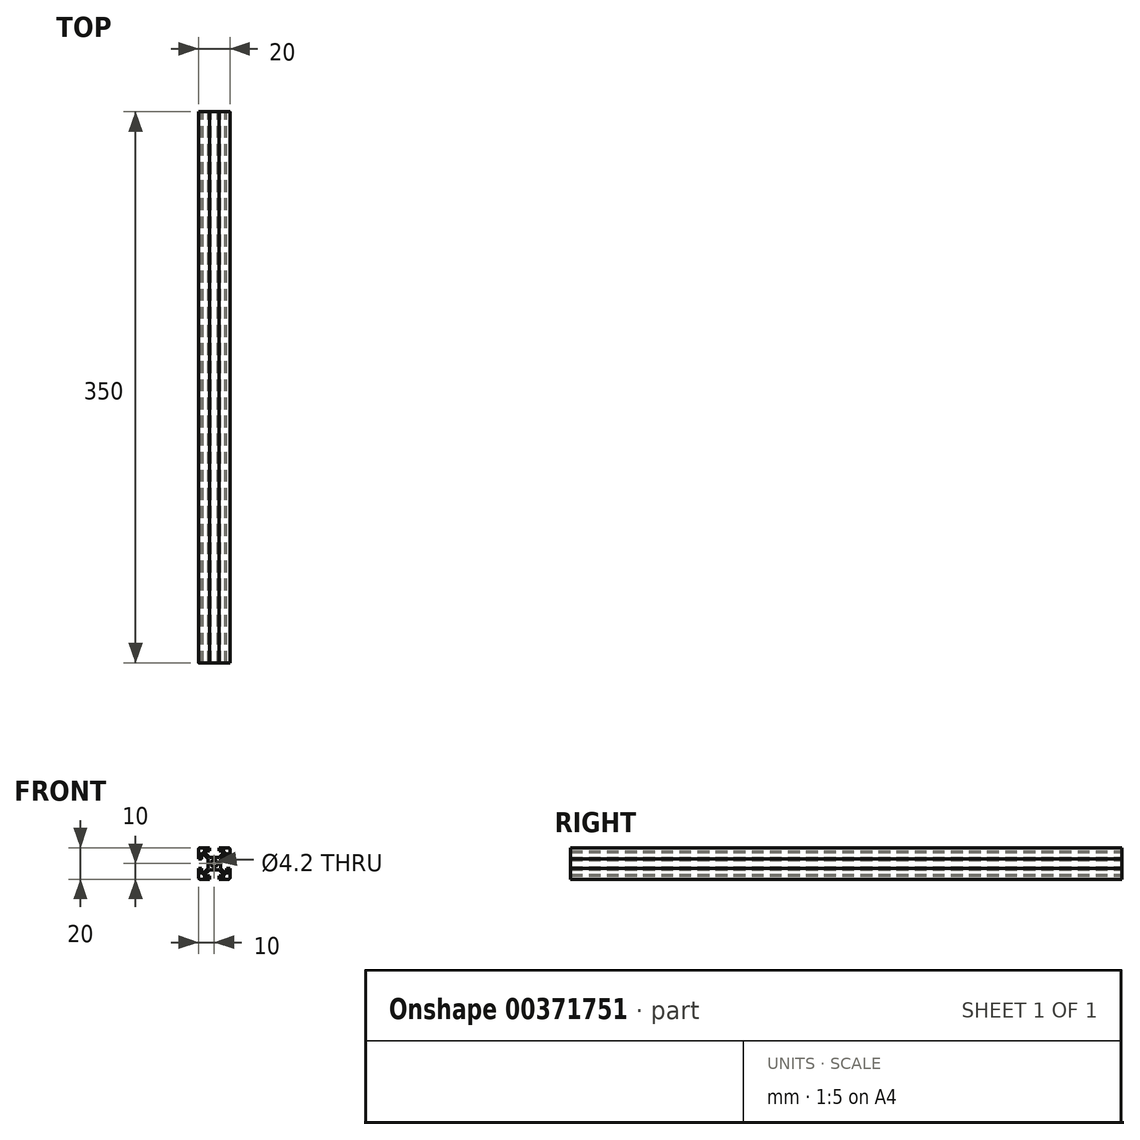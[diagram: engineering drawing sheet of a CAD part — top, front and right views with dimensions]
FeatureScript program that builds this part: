
annotation { "Feature Type Name" : "Feature", "Feature Type Description" : "" }
export const myFeature = defineFeature(function(context is Context, id is Id, definition is map)
    precondition{}
    {
        {
            var Q0;
            Q0=qCreatedBy(makeId("Front.planeOp"),FACE);
            var sketch = newSketch(context, id + "F0", { "sketchPlane" : qUnion([Q0])});
            skLineSegment(sketch, "E0.top", {"start": v(-9, -10) * mm, "end": v(-3, -10) * mm});
            skLineSegment(sketch, "E0.left", {"start": v(-10, 9) * mm, "end": v(-10, 3.08) * mm});
            skLineSegment(sketch, "E0.right", {"start": v(10, 9) * mm, "end": v(10, 3.08) * mm});
            skPoint(sketch, "E0.middle", {"position": v(0, 0) * mm});
            skArc(sketch, "E1.filletArc", {"start": v(-9, 10) * mm, "mid": v(-9.7, 9.7) * mm, "end": v(-10, 9) * mm});
            skArc(sketch, "E2.filletArc", {"start": v(10, 9) * mm, "mid": v(9.7, 9.7) * mm, "end": v(9, 10) * mm});
            skPoint(sketch, "E3.visualSharp", {"position": v(10, -10) * mm});
            skArc(sketch, "E3.filletArc", {"start": v(9, -10) * mm, "mid": v(9.7, -9.7) * mm, "end": v(10, -9) * mm});
            skArc(sketch, "E4.filletArc", {"start": v(-10, -9) * mm, "mid": v(-9.7, -9.7) * mm, "end": v(-9, -10) * mm});
            skCircle(sketch, "E5", {"center": v(0, 0) * mm, "radius": 2.1 * mm});
            skLineSegment(sketch, "E6.bottom", {"start": v(-3, 4) * mm, "end": v(3, 4) * mm});
            skLineSegment(sketch, "E6.top", {"start": v(-3, -4) * mm, "end": v(3, -4) * mm});
            skLineSegment(sketch, "E6.left", {"start": v(-4, 3) * mm, "end": v(-4, -3) * mm});
            skLineSegment(sketch, "E6.right", {"start": v(4, 3) * mm, "end": v(4, -3) * mm});
            skLineSegment(sketch, "E7", {"start": v(-4, 3) * mm, "end": v(-8, 7) * mm});
            skLineSegment(sketch, "E8", {"start": v(-7, 8) * mm, "end": v(-3, 4) * mm});
            skLineSegment(sketch, "E9", {"start": v(3, 4) * mm, "end": v(7, 8) * mm});
            skLineSegment(sketch, "E10", {"start": v(4, 3) * mm, "end": v(8, 7) * mm});
            skLineSegment(sketch, "E11", {"start": v(4, -3) * mm, "end": v(8, -7) * mm});
            skLineSegment(sketch, "E12", {"start": v(3, -4) * mm, "end": v(7, -8) * mm});
            skLineSegment(sketch, "E13", {"start": v(-3, -4) * mm, "end": v(-7, -8) * mm});
            skLineSegment(sketch, "E14", {"start": v(-8, -7) * mm, "end": v(-4, -3) * mm});
            skLineSegment(sketch, "E15.bottom", {"start": v(-7, 8) * mm, "end": v(-3, 8) * mm});
            skLineSegment(sketch, "E15.top", {"start": v(-7, -8) * mm, "end": v(-3, -8) * mm});
            skLineSegment(sketch, "E15.left", {"start": v(-8, 7) * mm, "end": v(-8, 3.18) * mm});
            skLineSegment(sketch, "E15.right", {"start": v(8, 7) * mm, "end": v(8, 3.08) * mm});
            skLineSegment(sketch, "E16", {"start": v(-3, -8) * mm, "end": v(-3, -10) * mm});
            skLineSegment(sketch, "E17", {"start": v(3, -8) * mm, "end": v(3, -10) * mm});
            skLineSegment(sketch, "E18", {"start": v(8, 3.08) * mm, "end": v(10, 3.08) * mm});
            skLineSegment(sketch, "E19", {"start": v(8, -3) * mm, "end": v(10, -3) * mm});
            skLineSegment(sketch, "E20", {"start": v(-3, 10) * mm, "end": v(-3, 8) * mm});
            skLineSegment(sketch, "E21", {"start": v(3, 10) * mm, "end": v(3, 8) * mm});
            skLineSegment(sketch, "E22", {"start": v(-10, 3.08) * mm, "end": v(-8.1, 3.08) * mm});
            skLineSegment(sketch, "E23", {"start": v(-10, -3) * mm, "end": v(-8, -3) * mm});
            skLineSegment(sketch, "E24.trimOffspring", {"start": v(-8, -3) * mm, "end": v(-8, -7) * mm});
            skLineSegment(sketch, "E25.trimOffspring", {"start": v(-10, -3) * mm, "end": v(-10, -9) * mm});
            skLineSegment(sketch, "E26.trimOffspring", {"start": v(3, 10) * mm, "end": v(9, 10) * mm});
            skLineSegment(sketch, "E27.trimOffspring", {"start": v(3, 8) * mm, "end": v(7, 8) * mm});
            skLineSegment(sketch, "E28", {"start": v(-9, 10) * mm, "end": v(-3, 10) * mm});
            skLineSegment(sketch, "E29.trimOffspring", {"start": v(10, -3) * mm, "end": v(10, -9) * mm});
            skLineSegment(sketch, "E30.trimOffspring", {"start": v(8, -3) * mm, "end": v(8, -7) * mm});
            skLineSegment(sketch, "E31.trimOffspring", {"start": v(3, -10) * mm, "end": v(9, -10) * mm});
            skLineSegment(sketch, "E32.trimOffspring", {"start": v(3, -8) * mm, "end": v(7, -8) * mm});
            skPoint(sketch, "E33.visualSharp", {"position": v(-8, 3.08) * mm});
            skArc(sketch, "E33.filletArc", {"start": v(-8.1, 3.08) * mm, "mid": v(-8.03, 3.1) * mm, "end": v(-8, 3.18) * mm});
            skSolve(sketch);
        }
        {
            assignVariable(context, id + "F1", {"name" : "x", "anyValue" : 350});
        }
        {
            var Q0;
            Q0=makeQuery(id+"F0.imprint","IMPRINT",FACE,{"disambiguationData":[TD([[makeQuery(id+"F0.imprint","IMPRINT",EDGE,{"derivedFrom":sQuery(id+"F0.wireOp",EDGE,"E0.top")}),1.0]])]});
            extrude(context, id + "F2", {"entities" : qUnion([Q0]), "depth" : (getVariable(context, 'x')) * mm});
        }
    });
